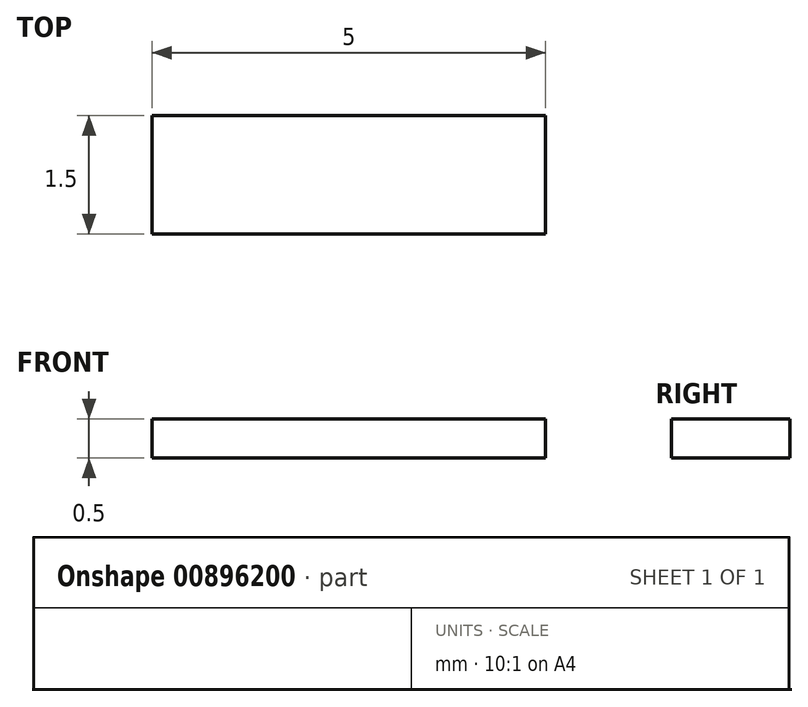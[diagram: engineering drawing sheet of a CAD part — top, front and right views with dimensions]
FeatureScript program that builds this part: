
annotation { "Feature Type Name" : "Feature", "Feature Type Description" : "" }
export const myFeature = defineFeature(function(context is Context, id is Id, definition is map)
    precondition{}
    {
        {
            var Q0;
            Q0=qCreatedBy(makeId("Top.planeOp"),FACE);
            var sketch = newSketch(context, id + "F0", { "sketchPlane" : qUnion([Q0])});
            skLineSegment(sketch, "E0.bottom", {"start": v(2.5, 0.75) * mm, "end": v(-2.5, 0.75) * mm});
            skLineSegment(sketch, "E0.top", {"start": v(2.5, -0.75) * mm, "end": v(-2.5, -0.75) * mm});
            skLineSegment(sketch, "E0.left", {"start": v(2.5, 0.75) * mm, "end": v(2.5, -0.75) * mm});
            skLineSegment(sketch, "E0.right", {"start": v(-2.5, 0.75) * mm, "end": v(-2.5, -0.75) * mm});
            skPoint(sketch, "E0.middle", {"position": v(0, 0) * mm});
            skSolve(sketch);
        }
        {
            var Q0;
            Q0 = qSketchRegion(id + "F0", true);
            extrude(context, id + "F1", {"entities" : qUnion([Q0]), "depth" : 0.5 * mm, "offsetDistance" : 25 * mm});
        }
    });
